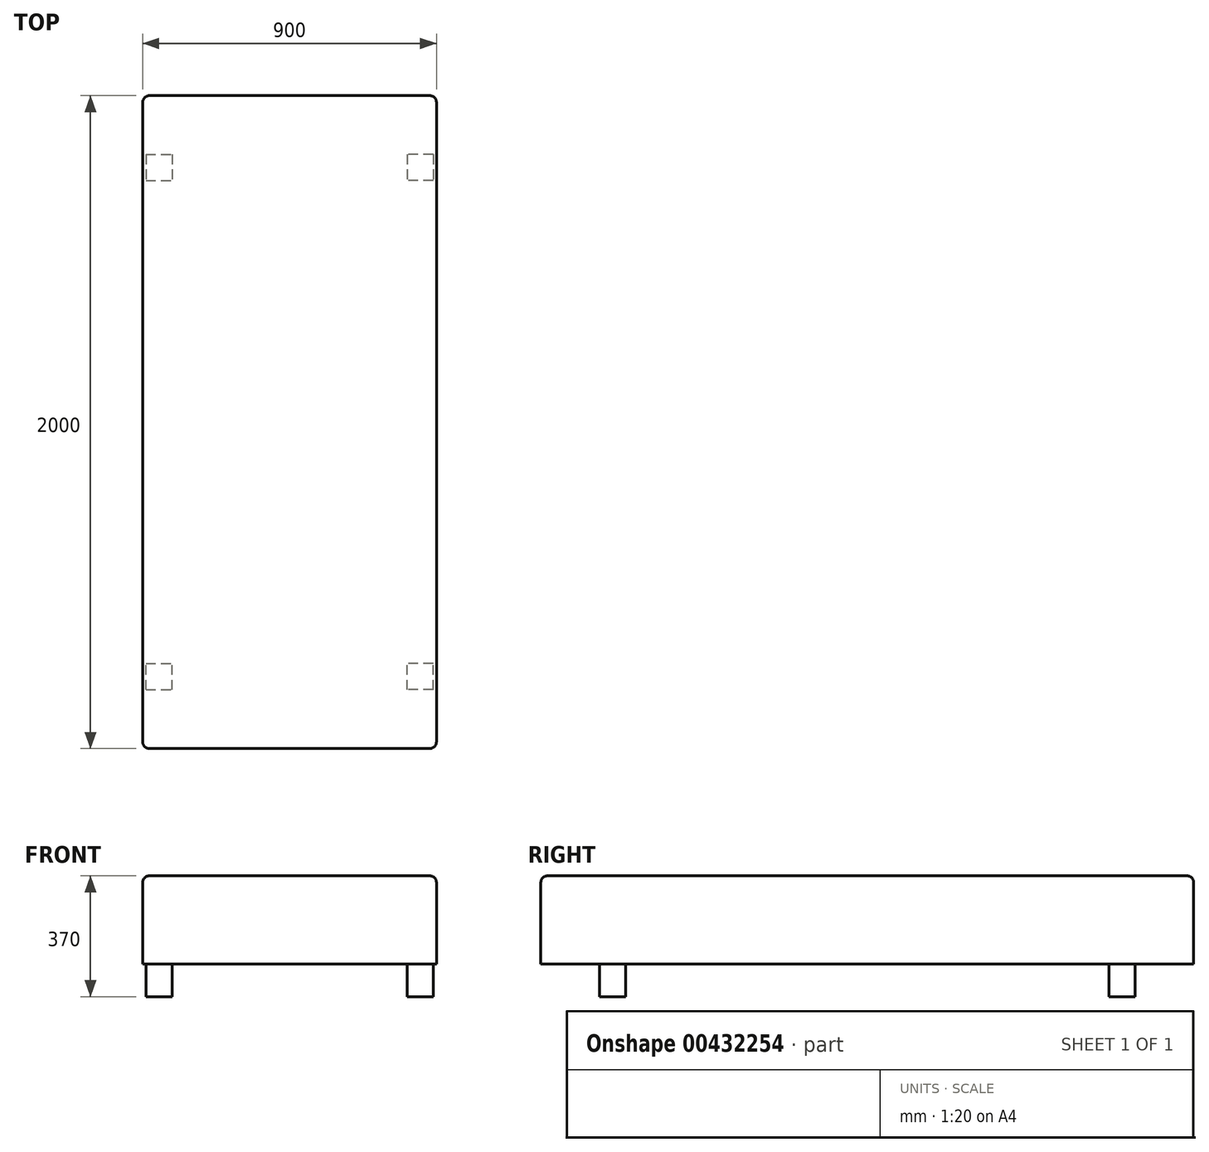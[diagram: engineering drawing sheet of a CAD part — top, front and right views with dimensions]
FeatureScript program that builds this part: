
annotation { "Feature Type Name" : "Feature", "Feature Type Description" : "" }
export const myFeature = defineFeature(function(context is Context, id is Id, definition is map)
    precondition{}
    {
        {
            var Q0;
            Q0=qCreatedBy(makeId("Top.planeOp"),FACE);
            var sketch = newSketch(context, id + "F0", { "sketchPlane" : qUnion([Q0])});
            skLineSegment(sketch, "E0.bottom", {"start": v(450, -1000) * mm, "end": v(-450, -1000) * mm});
            skLineSegment(sketch, "E0.top", {"start": v(450, 1000) * mm, "end": v(-450, 1000) * mm});
            skLineSegment(sketch, "E0.left", {"start": v(450, -1000) * mm, "end": v(450, 1000) * mm});
            skLineSegment(sketch, "E0.right", {"start": v(-450, -1000) * mm, "end": v(-450, 1000) * mm});
            skPoint(sketch, "E0.middle", {"position": v(0, 0) * mm});
            skSolve(sketch);
        }
        {
            var Q0;
            Q0 = qSketchRegion(id + "F0", true);
            extrude(context, id + "F1", {"entities" : qUnion([Q0]), "depth" : 270 * mm});
        }
        {
            var Q0;
            Q0=makeQuery(id+"F1.opExtrude","CAP_EDGE",EDGE,{"disambiguationData":[OSD([sQuery(id+"F0.wireOp",EDGE,"E0.right")])],"isStart":false});
            var Q1;
            Q1=makeQuery(id+"F1.opExtrude","CAP_EDGE",EDGE,{"disambiguationData":[OSD([sQuery(id+"F0.wireOp",EDGE,"E0.top")])],"isStart":false});
            var Q2;
            Q2=makeQuery(id+"F1.opExtrude","CAP_EDGE",EDGE,{"disambiguationData":[OSD([sQuery(id+"F0.wireOp",EDGE,"E0.left")])],"isStart":false});
            var Q3;
            Q3=makeQuery(id+"F1.opExtrude","CAP_EDGE",EDGE,{"disambiguationData":[OSD([sQuery(id+"F0.wireOp",EDGE,"E0.bottom")])],"isStart":false});
            var Q4;
            Q4=makeQuery(id+"F1.opExtrude","SWEPT_EDGE",EDGE,{"disambiguationData":[OSD([sQuery(id+"F0.wireOp",EDGE,"E0.bottom"),sQuery(id+"F0.wireOp",EDGE,"E0.left")])]});
            var Q5;
            Q5=makeQuery(id+"F1.opExtrude","SWEPT_EDGE",EDGE,{"disambiguationData":[OSD([sQuery(id+"F0.wireOp",EDGE,"E0.top"),sQuery(id+"F0.wireOp",EDGE,"E0.left")])]});
            var Q6;
            Q6=makeQuery(id+"F1.opExtrude","SWEPT_EDGE",EDGE,{"disambiguationData":[OSD([sQuery(id+"F0.wireOp",EDGE,"E0.top"),sQuery(id+"F0.wireOp",EDGE,"E0.right")])]});
            var Q7;
            Q7=makeQuery(id+"F1.opExtrude","SWEPT_EDGE",EDGE,{"disambiguationData":[OSD([sQuery(id+"F0.wireOp",EDGE,"E0.bottom"),sQuery(id+"F0.wireOp",EDGE,"E0.right")])]});
            fillet(context, id + "F2", {"entities" : qUnion([Q0, Q1, Q2, Q3, Q4, Q5, Q6, Q7]), "radius" : 20 * mm, "tangentPropagation" : true, "allowEdgeOverflow" : false});
        }
        {
            var Q0;
            Q0=makeQuery(id+"F1.opExtrude","CAP_FACE",FACE,{"disambiguationData":[OSD([sQuery(id+"F0.wireOp",EDGE,"E0.bottom"),sQuery(id+"F0.wireOp",EDGE,"E0.top"),sQuery(id+"F0.wireOp",EDGE,"E0.left"),sQuery(id+"F0.wireOp",EDGE,"E0.right")])],"isStart":true});
            var sketch = newSketch(context, id + "F3", { "sketchPlane" : qUnion([Q0])});
            skLineSegment(sketch, "E1.bottom", {"start": v(-440, 820) * mm, "end": v(-360, 820) * mm});
            skLineSegment(sketch, "E1.top", {"start": v(-440, 740) * mm, "end": v(-360, 740) * mm});
            skLineSegment(sketch, "E1.left", {"start": v(-440, 820) * mm, "end": v(-440, 740) * mm});
            skLineSegment(sketch, "E1.right", {"start": v(-360, 820) * mm, "end": v(-360, 740) * mm});
            skLineSegment(sketch, "E2.MirrorCS", {"start": v(440, 820) * mm, "end": v(360, 820) * mm});
            skLineSegment(sketch, "E3.MirrorCS", {"start": v(440, 740) * mm, "end": v(360, 740) * mm});
            skLineSegment(sketch, "E4.MirrorCS", {"start": v(440, 820) * mm, "end": v(440, 740) * mm});
            skLineSegment(sketch, "E5.MirrorCS", {"start": v(360, 820) * mm, "end": v(360, 740) * mm});
            skLineSegment(sketch, "E6.MirrorCS", {"start": v(360, -820) * mm, "end": v(360, -740) * mm});
            skLineSegment(sketch, "E7.MirrorCS", {"start": v(440, -820) * mm, "end": v(440, -740) * mm});
            skLineSegment(sketch, "E8.MirrorCS", {"start": v(440, -740) * mm, "end": v(360, -740) * mm});
            skLineSegment(sketch, "E9.MirrorCS", {"start": v(440, -820) * mm, "end": v(360, -820) * mm});
            skLineSegment(sketch, "E10.MirrorCS", {"start": v(-360, -820) * mm, "end": v(-360, -740) * mm});
            skLineSegment(sketch, "E11.MirrorCS", {"start": v(-440, -820) * mm, "end": v(-440, -740) * mm});
            skLineSegment(sketch, "E12.MirrorCS", {"start": v(-440, -740) * mm, "end": v(-360, -740) * mm});
            skLineSegment(sketch, "E13.MirrorCS", {"start": v(-440, -820) * mm, "end": v(-360, -820) * mm});
            skSolve(sketch);
        }
        {
            var Q0;
            Q0=makeQuery(id+"F3.imprint","IMPRINT",FACE,{"disambiguationData":[TD([[makeQuery(id+"F3.imprint","IMPRINT",EDGE,{"derivedFrom":sQuery(id+"F3.wireOp",EDGE,"E1.bottom")}),-1.0]])]});
            var Q1;
            Q1=makeQuery(id+"F3.imprint","IMPRINT",FACE,{"disambiguationData":[TD([[makeQuery(id+"F3.imprint","IMPRINT",EDGE,{"derivedFrom":sQuery(id+"F3.wireOp",EDGE,"E2.MirrorCS")}),1.0]])]});
            var Q2;
            Q2=makeQuery(id+"F3.imprint","IMPRINT",FACE,{"disambiguationData":[TD([[makeQuery(id+"F3.imprint","IMPRINT",EDGE,{"derivedFrom":sQuery(id+"F3.wireOp",EDGE,"E6.MirrorCS")}),-1.0]])]});
            var Q3;
            Q3=makeQuery(id+"F3.imprint","IMPRINT",FACE,{"disambiguationData":[TD([[makeQuery(id+"F3.imprint","IMPRINT",EDGE,{"derivedFrom":sQuery(id+"F3.wireOp",EDGE,"E10.MirrorCS")}),1.0]])]});
            extrude(context, id + "F4", {"entities" : qUnion([Q0, Q1, Q2, Q3]), "operationType" : NewBodyOperationType.ADD, "depth" : 100 * mm});
        }
    });
